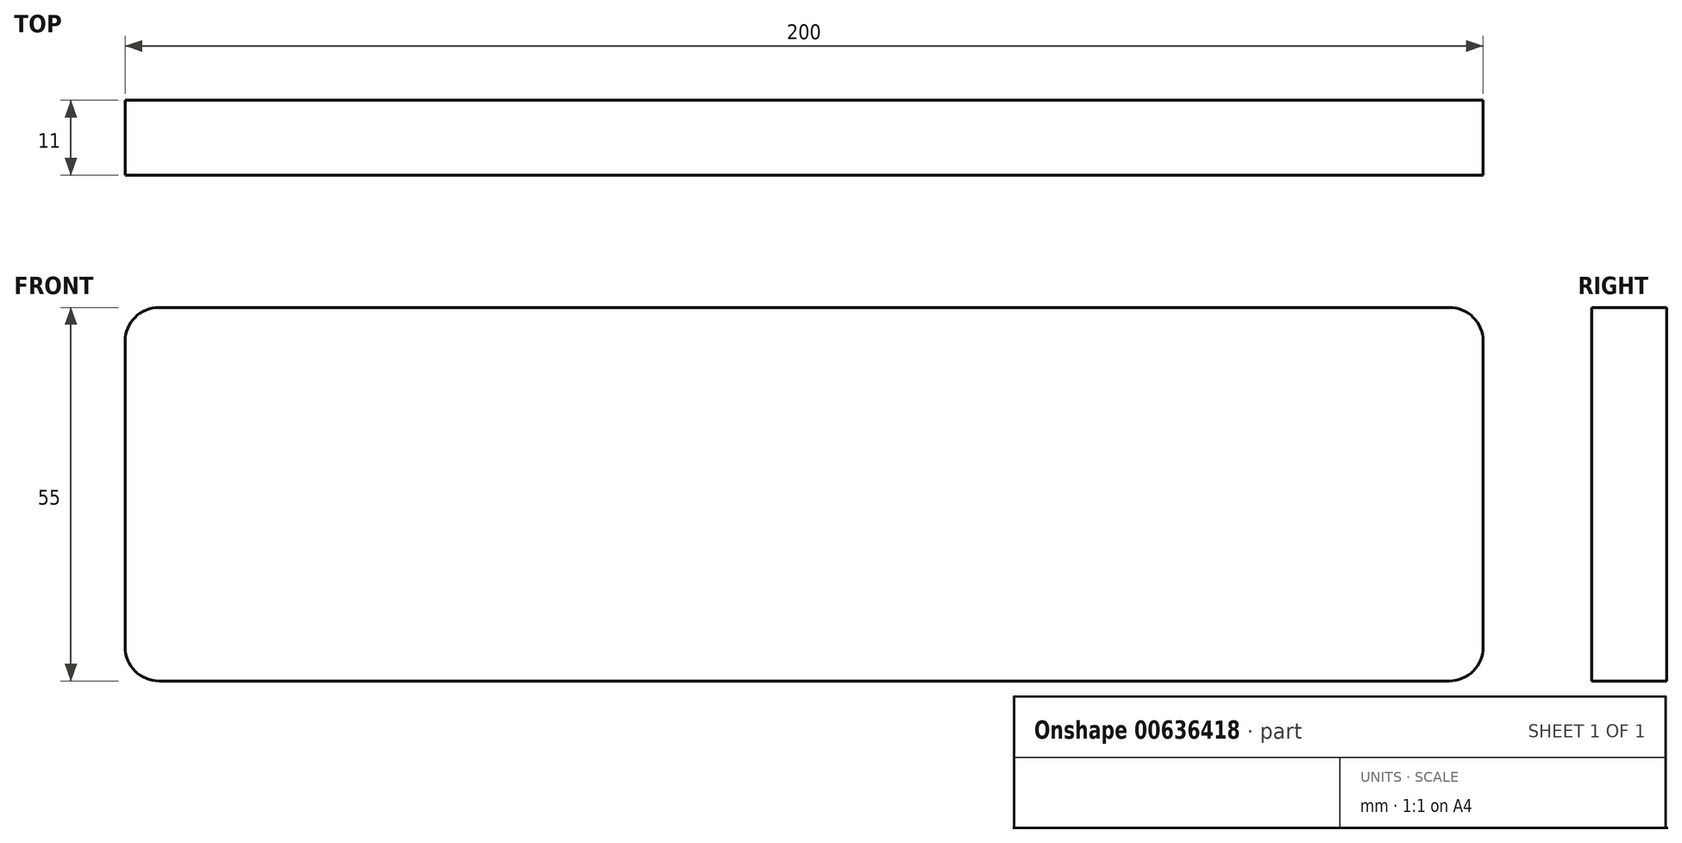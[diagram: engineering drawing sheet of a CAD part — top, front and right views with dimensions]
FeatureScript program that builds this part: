
annotation { "Feature Type Name" : "Feature", "Feature Type Description" : "" }
export const myFeature = defineFeature(function(context is Context, id is Id, definition is map)
    precondition{}
    {
        {
            var Q0;
            Q0=qCreatedBy(makeId("Front.planeOp"),FACE);
            var sketch = newSketch(context, id + "F0", { "sketchPlane" : qUnion([Q0])});
            skLineSegment(sketch, "E0.bottom", {"start": v(-56.44, 28.7) * mm, "end": v(133.56, 28.7) * mm});
            skLineSegment(sketch, "E0.top", {"start": v(-56.44, -26.3) * mm, "end": v(133.56, -26.3) * mm});
            skLineSegment(sketch, "E0.left", {"start": v(-61.44, 23.7) * mm, "end": v(-61.44, -21.3) * mm});
            skLineSegment(sketch, "E0.right", {"start": v(138.56, 23.7) * mm, "end": v(138.56, -21.3) * mm});
            skPoint(sketch, "E1.visualSharp", {"position": v(-61.44, 28.7) * mm});
            skArc(sketch, "E1.filletArc", {"start": v(-56.44, 28.7) * mm, "mid": v(-59.97, 27.24) * mm, "end": v(-61.44, 23.7) * mm});
            skPoint(sketch, "E2.visualSharp", {"position": v(138.56, 28.7) * mm});
            skArc(sketch, "E2.filletArc", {"start": v(138.56, 23.7) * mm, "mid": v(137.1, 27.24) * mm, "end": v(133.56, 28.7) * mm});
            skPoint(sketch, "E3.visualSharp", {"position": v(138.56, -26.3) * mm});
            skArc(sketch, "E3.filletArc", {"start": v(133.56, -26.3) * mm, "mid": v(137.1, -24.83) * mm, "end": v(138.56, -21.3) * mm});
            skPoint(sketch, "E4.visualSharp", {"position": v(-61.44, -26.3) * mm});
            skArc(sketch, "E4.filletArc", {"start": v(-61.44, -21.3) * mm, "mid": v(-59.97, -24.83) * mm, "end": v(-56.44, -26.3) * mm});
            skSolve(sketch);
        }
        {
            var Q0;
            Q0=makeQuery(id+"F0.imprint","IMPRINT",FACE,{"disambiguationData":[TD([[makeQuery(id+"F0.imprint","IMPRINT",EDGE,{"derivedFrom":sQuery(id+"F0.wireOp",EDGE,"E0.bottom")}),-1.0]])]});
            extrude(context, id + "F1", {"entities" : qUnion([Q0]), "depth" : 11 * mm, "offsetDistance" : 25 * mm});
        }
    });
